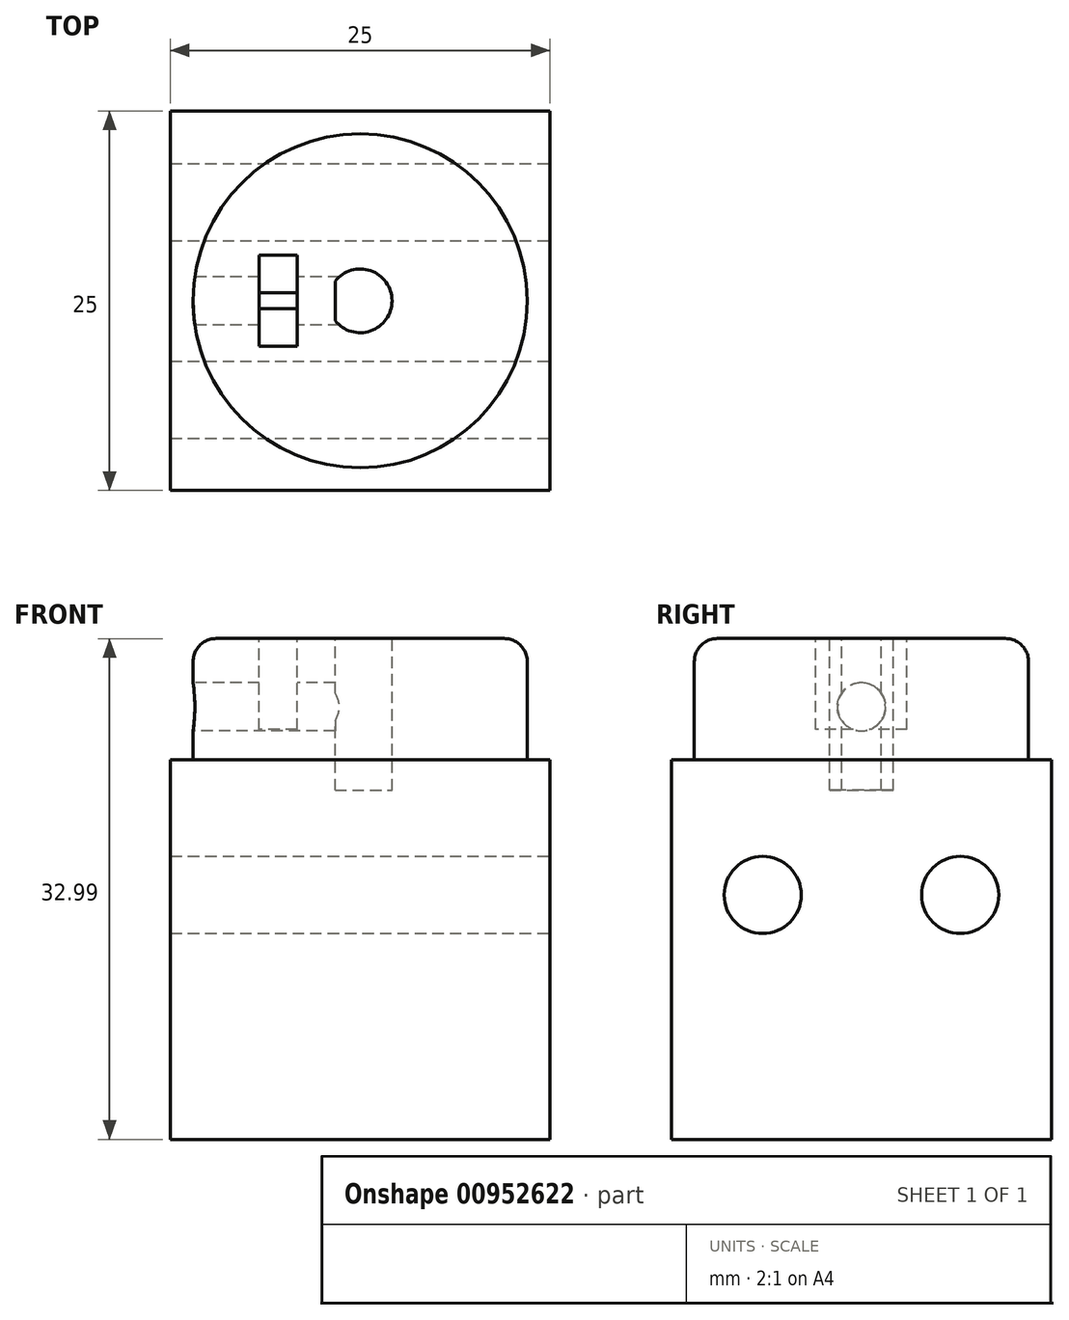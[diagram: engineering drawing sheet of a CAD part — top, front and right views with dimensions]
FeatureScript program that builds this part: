
annotation { "Feature Type Name" : "Feature", "Feature Type Description" : "" }
export const myFeature = defineFeature(function(context is Context, id is Id, definition is map)
    precondition{}
    {
        {
            var Q0;
            Q0=qCreatedBy(makeId("Top.planeOp"),FACE);
            var sketch = newSketch(context, id + "F0", { "sketchPlane" : qUnion([Q0])});
            skLineSegment(sketch, "E0.bottom", {"start": v(12.5, 12.5) * mm, "end": v(-12.5, 12.5) * mm});
            skLineSegment(sketch, "E0.top", {"start": v(12.5, -12.5) * mm, "end": v(-12.5, -12.5) * mm});
            skLineSegment(sketch, "E0.left", {"start": v(12.5, 12.5) * mm, "end": v(12.5, -12.5) * mm});
            skLineSegment(sketch, "E0.right", {"start": v(-12.5, 12.5) * mm, "end": v(-12.5, -12.5) * mm});
            skPoint(sketch, "E0.middle", {"position": v(0, 0) * mm});
            skSolve(sketch);
        }
        {
            var Q0;
            Q0 = qSketchRegion(id + "F0", true);
            extrude(context, id + "F1", {"entities" : qUnion([Q0]), "depth" : 25 * mm, "offsetDistance" : 25.4 * mm});
        }
        {
            var Q0;
            Q0=makeQuery(id+"F1.opExtrude","CAP_FACE",FACE,{"disambiguationData":[OSD([sQuery(id+"F0.wireOp",EDGE,"E0.bottom"),sQuery(id+"F0.wireOp",EDGE,"E0.top"),sQuery(id+"F0.wireOp",EDGE,"E0.left"),sQuery(id+"F0.wireOp",EDGE,"E0.right")])],"isStart":false});
            var sketch = newSketch(context, id + "F2", { "sketchPlane" : qUnion([Q0])});
            skCircle(sketch, "E1", {"center": v(0, 0) * mm, "radius": 11 * mm});
            skSolve(sketch);
        }
        {
            var Q0;
            Q0=makeQuery(id+"F2.imprint","IMPRINT",FACE,{"disambiguationData":[TD([[makeQuery(id+"F2.imprint","IMPRINT",EDGE,{"derivedFrom":sQuery(id+"F2.wireOp",EDGE,"E1")}),1.0]])]});
            var Q1;
            Q1 = qSketchRegion(id + "F2", true);
            extrude(context, id + "F3", {"entities" : qUnion([Q0, Q1]), "operationType" : NewBodyOperationType.ADD, "depth" : 8 * mm, "offsetDistance" : 25.4 * mm});
        }
        {
            var Q0;
            Q0=makeQuery(id+"F3.opExtrude","CAP_FACE",FACE,{"disambiguationData":[OSD([sQuery(id+"F2.wireOp",EDGE,"E1")])],"isStart":false});
            fillet(context, id + "F4", {"entities" : qUnion([Q0]), "radius" : 1.52 * mm, "tangentPropagation" : true, "allowEdgeOverflow" : false});
        }
        {
            var Q0;
            Q0=makeQuery(id+"F3.opExtrude","CAP_FACE",FACE,{"disambiguationData":[OSD([sQuery(id+"F2.wireOp",EDGE,"E1")])],"isStart":false});
            var sketch = newSketch(context, id + "F5", { "sketchPlane" : qUnion([Q0])});
            skArc(sketch, "E2", {"start": v(-1.65, -1.3) * mm, "mid": v(2.1, 0) * mm, "end": v(-1.65, 1.3) * mm});
            skLineSegment(sketch, "E3", {"start": v(-1.65, 1.3) * mm, "end": v(-1.65, -1.3) * mm});
            skPoint(sketch, "E4.orphan", {"position": v(-1.65, 0) * mm});
            skPoint(sketch, "E5.middle", {"position": v(-3.7, 0) * mm});
            skPoint(sketch, "E6.start.orphan", {"position": v(2.1, 0) * mm});
            skLineSegment(sketch, "E7", {"start": v(-1.65, 0) * mm, "end": v(2.1, 0) * mm});
            skLineSegment(sketch, "E8", {"start": v(-1.65, 0) * mm, "end": v(-10.04, 0) * mm});
            skSolve(sketch);
        }
        {
            var Q0;
            Q0 = qSketchRegion(id + "F5", true);
            extrude(context, id + "F6", {"entities" : qUnion([Q0]), "operationType" : NewBodyOperationType.REMOVE, "oppositeDirection" : true, "depth" : 10 * mm, "offsetDistance" : 25.4 * mm});
        }
        {
            var Q0;
            Q0=makeQuery(id+"F3.opExtrude","CAP_FACE",FACE,{"disambiguationData":[OSD([sQuery(id+"F2.wireOp",EDGE,"E1")])],"isStart":false});
            var sketch = newSketch(context, id + "F7", { "sketchPlane" : qUnion([Q0])});
            skLineSegment(sketch, "E9.bottom", {"start": v(-4.15, 3) * mm, "end": v(-6.65, 3) * mm});
            skLineSegment(sketch, "E9.top", {"start": v(-4.15, -3) * mm, "end": v(-6.65, -3) * mm});
            skLineSegment(sketch, "E9.left", {"start": v(-4.15, 3) * mm, "end": v(-4.15, -3) * mm});
            skLineSegment(sketch, "E9.right", {"start": v(-6.65, 3) * mm, "end": v(-6.65, -3) * mm});
            skPoint(sketch, "E9.middle", {"position": v(-5.4, 0) * mm});
            skLineSegment(sketch, "E10", {"start": v(-4.15, 0) * mm, "end": v(-1.65, 0) * mm});
            skSolve(sketch);
        }
        {
            var Q0;
            Q0 = qSketchRegion(id + "F7", true);
            extrude(context, id + "F8", {"entities" : qUnion([Q0]), "operationType" : NewBodyOperationType.REMOVE, "oppositeDirection" : true, "depth" : 6 * mm, "offsetDistance" : 25.4 * mm});
        }
        {
            var Q0;
            Q0=makeQuery(id+"F1.opExtrude","SWEPT_FACE",FACE,{"disambiguationData":[OSD([sQuery(id+"F0.wireOp",EDGE,"E0.right")])]});
            var sketch = newSketch(context, id + "F9", { "sketchPlane" : qUnion([Q0])});
            skPoint(sketch, "E11.startSnap0", {"position": v(0, 25) * mm});
            skCircle(sketch, "E12", {"center": v(0, 28.5) * mm, "radius": 1.59 * mm});
            skPoint(sketch, "E13.orphan", {"position": v(0, 32) * mm});
            skPoint(sketch, "E11.end.orphan", {"position": v(0, 25) * mm});
            skSolve(sketch);
        }
        {
            var Q0;
            Q0 = qSketchRegion(id + "F9", true);
            extrude(context, id + "F10", {"entities" : qUnion([Q0]), "operationType" : NewBodyOperationType.REMOVE, "oppositeDirection" : true, "depth" : 11.68 * mm, "offsetDistance" : 25.4 * mm});
        }
        {
            var Q0;
            Q0=makeQuery(id+"F1.opExtrude","SWEPT_FACE",FACE,{"disambiguationData":[OSD([sQuery(id+"F0.wireOp",EDGE,"E0.left")])]});
            var sketch = newSketch(context, id + "F11", { "sketchPlane" : qUnion([Q0])});
            skPoint(sketch, "E14.orphan", {"position": v(6.5, 25) * mm});
            skPoint(sketch, "E15.start.orphan", {"position": v(6.5, 7.21) * mm});
            skCircle(sketch, "E16", {"center": v(-6.5, 16.1) * mm, "radius": 2.54 * mm});
            skCircle(sketch, "E17", {"center": v(6.5, 16.1) * mm, "radius": 2.54 * mm});
            skSolve(sketch);
        }
        {
            var Q0;
            Q0 = qSketchRegion(id + "F11", true);
            extrude(context, id + "F12", {"entities" : qUnion([Q0]), "operationType" : NewBodyOperationType.REMOVE, "oppositeDirection" : true, "depth" : 25.4 * mm, "offsetDistance" : 25.4 * mm});
        }
    });
